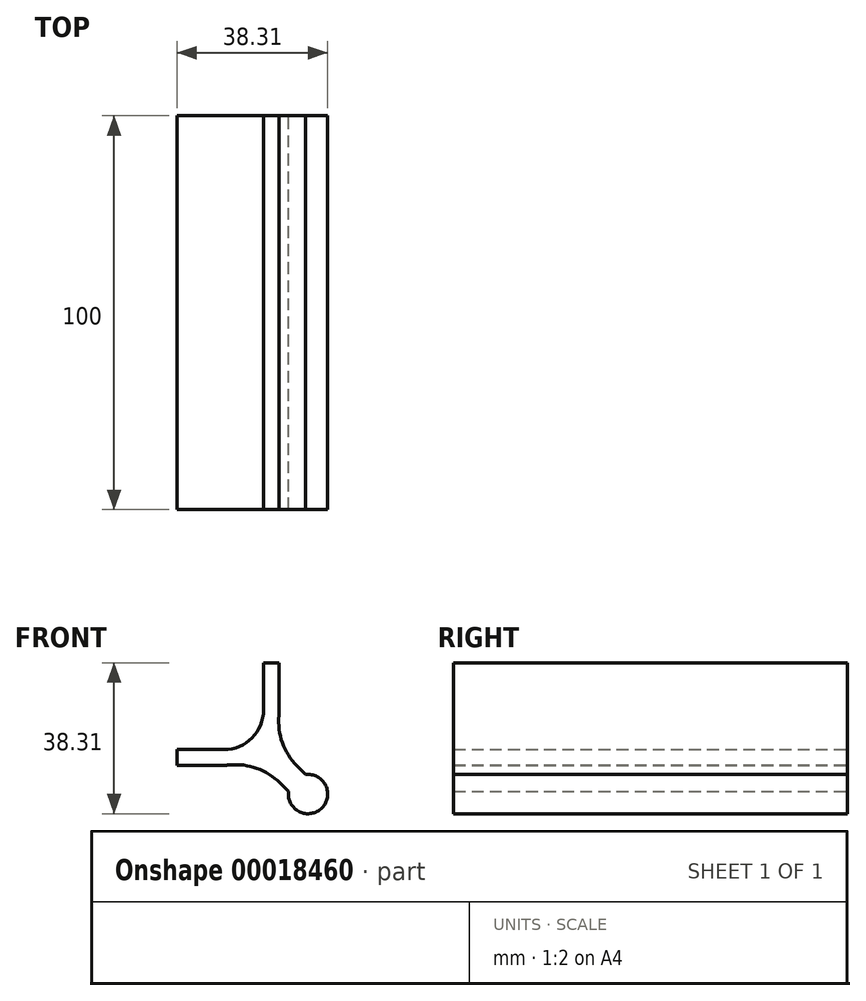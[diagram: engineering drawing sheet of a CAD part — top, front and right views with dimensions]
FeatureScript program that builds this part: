
annotation { "Feature Type Name" : "Feature", "Feature Type Description" : "" }
export const myFeature = defineFeature(function(context is Context, id is Id, definition is map)
    precondition{}
    {
        {
            var Q0;
            Q0=qCreatedBy(makeId("Front.planeOp"),FACE);
            var sketch = newSketch(context, id + "F0", { "sketchPlane" : qUnion([Q0])});
            skLineSegment(sketch, "E0", {"start": v(0, 22) * mm, "end": v(0, 10) * mm});
            skLineSegment(sketch, "E1", {"start": v(-10, 0) * mm, "end": v(-22, 0) * mm});
            skArc(sketch, "E2.filletArc", {"start": v(-10, 0) * mm, "mid": v(-2.93, 2.93) * mm, "end": v(0, 10) * mm});
            skLineSegment(sketch, "E3.0", {"start": v(-10, -4) * mm, "end": v(-22, -4) * mm});
            skArc(sketch, "E3.1", {"start": v(-10, -4) * mm, "mid": v(-0.1, 0.1) * mm, "end": v(4, 10) * mm});
            skLineSegment(sketch, "E3.2", {"start": v(4, 22) * mm, "end": v(4, 10) * mm});
            skLineSegment(sketch, "E4", {"start": v(0, 22) * mm, "end": v(4, 22) * mm});
            skLineSegment(sketch, "E5", {"start": v(-22, 0) * mm, "end": v(-22, -4) * mm});
            skLineSegment(sketch, "E6", {"start": v(-10, 10) * mm, "end": v(0, 0) * mm, "construction": true});
            skLineSegment(sketch, "E7", {"start": v(0, 0) * mm, "end": v(14.85, -14.85) * mm, "construction": true});
            skLineSegment(sketch, "E8", {"start": v(14.85, -14.85) * mm, "end": v(26.85, -2.85) * mm, "construction": true});
            skLineSegment(sketch, "E9", {"start": v(14.85, -14.85) * mm, "end": v(6.82, -22.88) * mm, "construction": true});
            skCircle(sketch, "E10", {"center": v(11.31, -11.31) * mm, "radius": 5 * mm});
            skLineSegment(sketch, "E11", {"start": v(6.35, -10.7) * mm, "end": v(-2.51, -1.83) * mm});
            skLineSegment(sketch, "E12", {"start": v(1.83, 2.51) * mm, "end": v(10.7, -6.35) * mm});
            skSolve(sketch);
        }
        {
            var Q0;
            Q0=makeQuery(id+"F0.imprint","IMPRINT",FACE,{"disambiguationData":[TD([[makeQuery(id+"F0.imprint","IMPRINT",EDGE,{"derivedFrom":sQuery(id+"F0.wireOp",EDGE,"E0")}),1.0]])]});
            var Q1;
            {var subQ1=sQuery(id+"F0.wireOp",EDGE,"E11");Q1=makeQuery(id+"F0.imprint","IMPRINT",FACE,{"disambiguationData":[TD([[makeQuery(id+"F0.imprint","IMPRINT",EDGE,{"derivedFrom":subQ1}),-1.0]])]});}
            var Q2;
            {var subQ0=sQuery(id+"F0.wireOp",EDGE,"E10");var subQ2=makeQuery(id+"F0.imprint","INTERSECT",VERTEX,{"derivedFrom":[subQ0,sQuery(id+"F0.wireOp",EDGE,"E11")]});Q2=makeQuery(id+"F0.imprint","IMPRINT",FACE,{"disambiguationData":[TD([[makeQuery(id+"F0.imprint","IMPRINT",EDGE,{"disambiguationData":[TD([[subQ2,1.0]])],"derivedFrom":subQ0}),1.0]])]});}
            extrude(context, id + "F1", {"entities" : qUnion([Q0, Q1, Q2]), "depth" : 100 * mm});
        }
        {
            var Q0;
            Q0=makeQuery(id+"F1.opExtrude","SWEPT_EDGE",EDGE,{"disambiguationData":[OSD([sQuery(id+"F0.wireOp",EDGE,"E3.1"),sQuery(id+"F0.wireOp",EDGE,"E12")])]});
            var Q1;
            Q1=makeQuery(id+"F1.opExtrude","SWEPT_EDGE",EDGE,{"disambiguationData":[OSD([sQuery(id+"F0.wireOp",EDGE,"E3.1"),sQuery(id+"F0.wireOp",EDGE,"E11")])]});
            fillet(context, id + "F2", {"entities" : qUnion([Q0, Q1]), "radius" : 15.88 * mm, "tangentPropagation" : true, "allowEdgeOverflow" : false});
        }
    });
